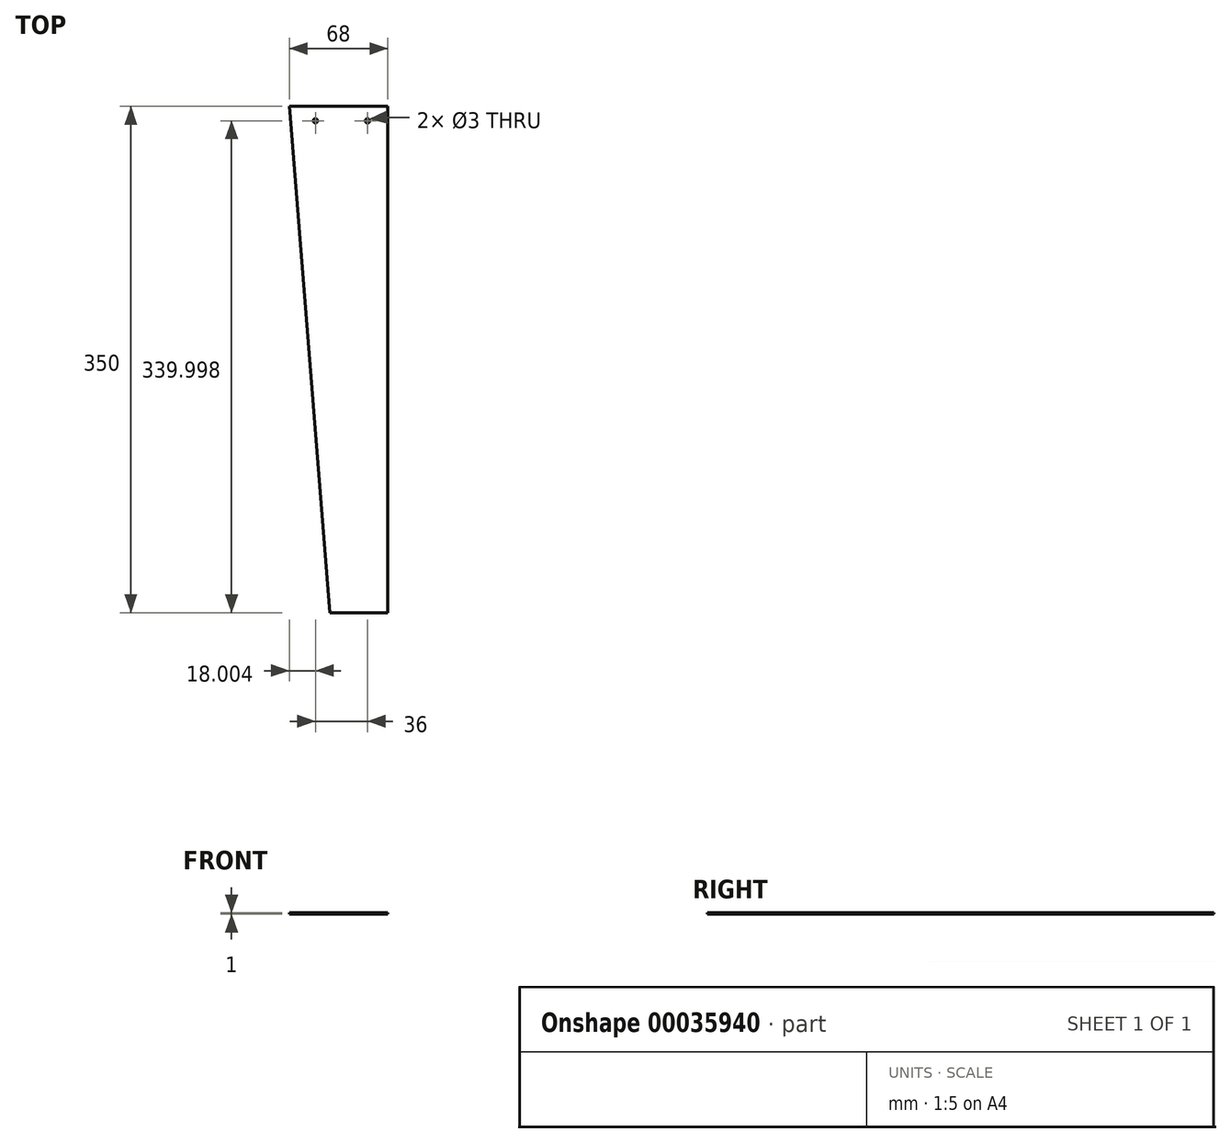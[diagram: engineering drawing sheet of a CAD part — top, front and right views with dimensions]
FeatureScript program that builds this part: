
annotation { "Feature Type Name" : "Feature", "Feature Type Description" : "" }
export const myFeature = defineFeature(function(context is Context, id is Id, definition is map)
    precondition{}
    {
        {
            var Q0;
            Q0=qCreatedBy(makeId("Top.planeOp"),FACE);
            var sketch = newSketch(context, id + "F0", { "sketchPlane" : qUnion([Q0])});
            skLineSegment(sketch, "E0.bottom", {"start": v(-48.17, 172.25) * mm, "end": v(19.83, 172.25) * mm});
            skLineSegment(sketch, "E0.top", {"start": v(-20.17, -177.75) * mm, "end": v(19.83, -177.75) * mm});
            skLineSegment(sketch, "E0.right", {"start": v(19.83, 172.25) * mm, "end": v(19.83, -177.75) * mm});
            skLineSegment(sketch, "E1", {"start": v(-20.17, -195.97) * mm, "end": v(-20.17, -143.38) * mm, "construction": true});
            skLineSegment(sketch, "E2", {"start": v(-20.17, -177.75) * mm, "end": v(-48.17, 172.25) * mm});
            skLineSegment(sketch, "E3", {"start": v(-81.04, 162.25) * mm, "end": v(52.46, 162.25) * mm, "construction": true});
            skLineSegment(sketch, "E4", {"start": v(5.83, 181.4) * mm, "end": v(5.83, 148.9) * mm, "construction": true});
            skLineSegment(sketch, "E5", {"start": v(-30.17, 179.3) * mm, "end": v(-30.17, 147.2) * mm, "construction": true});
            skCircle(sketch, "E6", {"center": v(-30.17, 162.25) * mm, "radius": 1.5 * mm});
            skCircle(sketch, "E7", {"center": v(5.83, 162.25) * mm, "radius": 1.5 * mm});
            skSolve(sketch);
        }
        {
            var Q0;
            Q0=makeQuery(id+"F0.imprint","IMPRINT",FACE,{"disambiguationData":[TD([[makeQuery(id+"F0.imprint","IMPRINT",EDGE,{"derivedFrom":sQuery(id+"F0.wireOp",EDGE,"E0.bottom")}),-1.0]])]});
            extrude(context, id + "F1", {"entities" : qUnion([Q0]), "depth" : 1 * mm});
        }
    });
